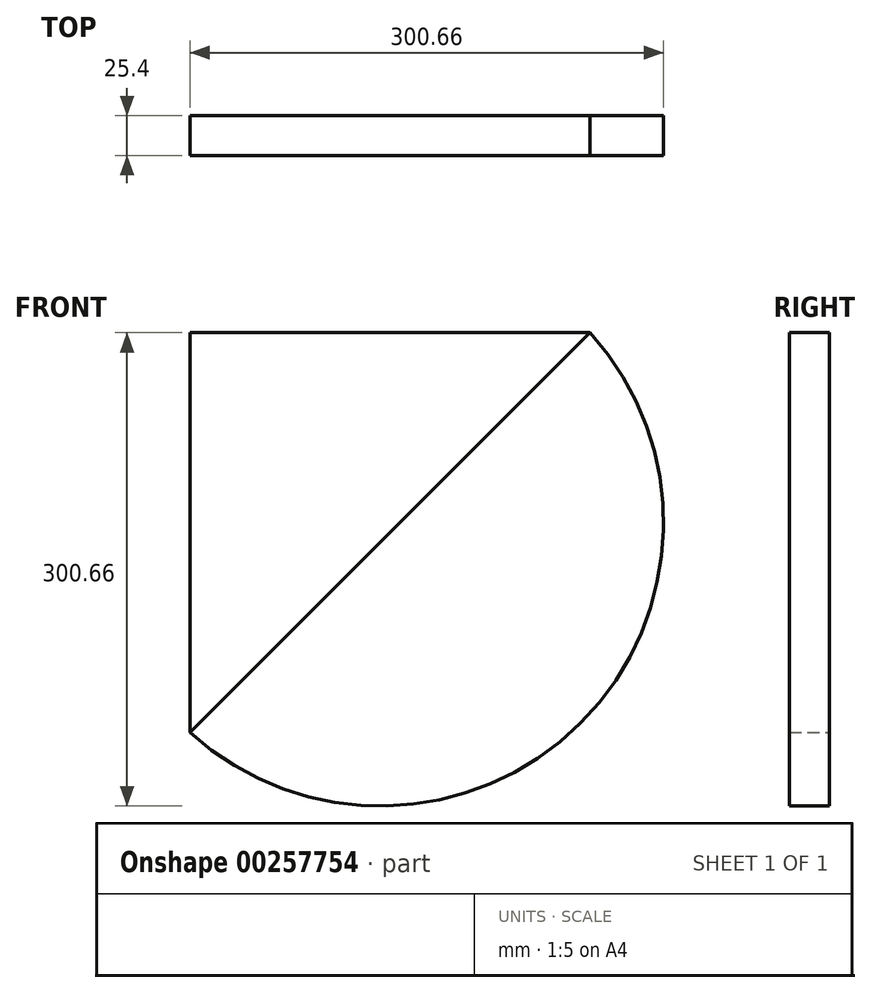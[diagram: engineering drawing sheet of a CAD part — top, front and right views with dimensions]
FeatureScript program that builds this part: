
annotation { "Feature Type Name" : "Feature", "Feature Type Description" : "" }
export const myFeature = defineFeature(function(context is Context, id is Id, definition is map)
    precondition{}
    {
        {
            var Q0;
            Q0=qCreatedBy(makeId("Front.planeOp"),FACE);
            var sketch = newSketch(context, id + "F0", { "sketchPlane" : qUnion([Q0])});
            skLineSegment(sketch, "E0.top", {"start": v(127, 127) * mm, "end": v(-127, 127) * mm});
            skLineSegment(sketch, "E0.right", {"start": v(-127, -127) * mm, "end": v(-127, 127) * mm});
            skPoint(sketch, "E0.middle", {"position": v(0, 0) * mm});
            skLineSegment(sketch, "E1", {"start": v(127, 127) * mm, "end": v(-127, -127) * mm});
            skPoint(sketch, "E0.bottom.start.orphan", {"position": v(127, -127) * mm});
            skArc(sketch, "E2", {"start": v(-127, -127) * mm, "mid": v(121, -121) * mm, "end": v(127, 127) * mm});
            skSolve(sketch);
        }
        {
            var Q0;
            Q0=makeQuery(id+"F0.imprint","IMPRINT",FACE,{"disambiguationData":[TD([[makeQuery(id+"F0.imprint","IMPRINT",EDGE,{"derivedFrom":sQuery(id+"F0.wireOp",EDGE,"E0.top")}),1.0]])]});
            extrude(context, id + "F1", {"entities" : qUnion([Q0]), "depth" : 25.4 * mm});
        }
        {
            var Q0;
            Q0=makeQuery(id+"F0.imprint","IMPRINT",FACE,{"disambiguationData":[TD([[makeQuery(id+"F0.imprint","IMPRINT",EDGE,{"derivedFrom":sQuery(id+"F0.wireOp",EDGE,"E1")}),1.0]])]});
            extrude(context, id + "F2", {"entities" : qUnion([Q0]), "depth" : 25.4 * mm});
        }
    });
